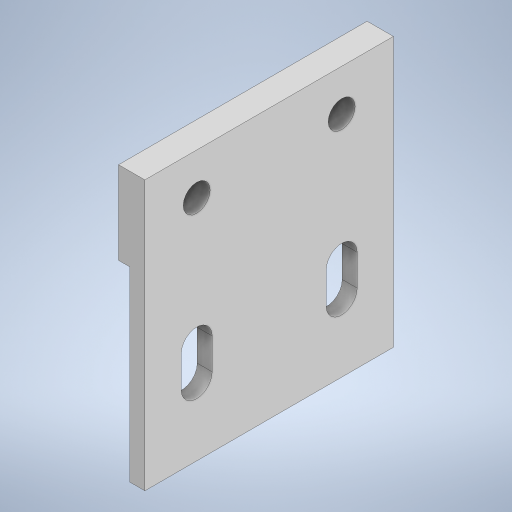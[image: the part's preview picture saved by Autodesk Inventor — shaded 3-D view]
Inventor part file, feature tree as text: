
AUTODESK INVENTOR PART (.ipt)
format: ipt  version: 2023 (Build 270158000, 158)  size: 240,640 bytes
history: native  units: mm
features: extrude x2, sketch x1
ambient origin geometry x8: Origin, YZ Plane, XZ Plane, XY Plane, X Axis, Y Axis, Z Axis, Center Point
bodies: Solid1 (feature_tree)
feature tree (3):
  sketch  "Sketch1"  dims[d1=60.0mm d4=7.5mm d5=7.5mm d8=8.75mm d10=35.0mm d12=6.35mm d13=0.0mm d15=10.0mm d16=6.5mm d17=6.5mm d18=30.75mm d19=65.0mm d20=7.5mm d21=20.0mm d22=2.75mm d23=0.0mm]
  extrude  "Extrusion1"  Depth=7.5mm
  extrude  "Extrusion2"  Depth=7.5mm
